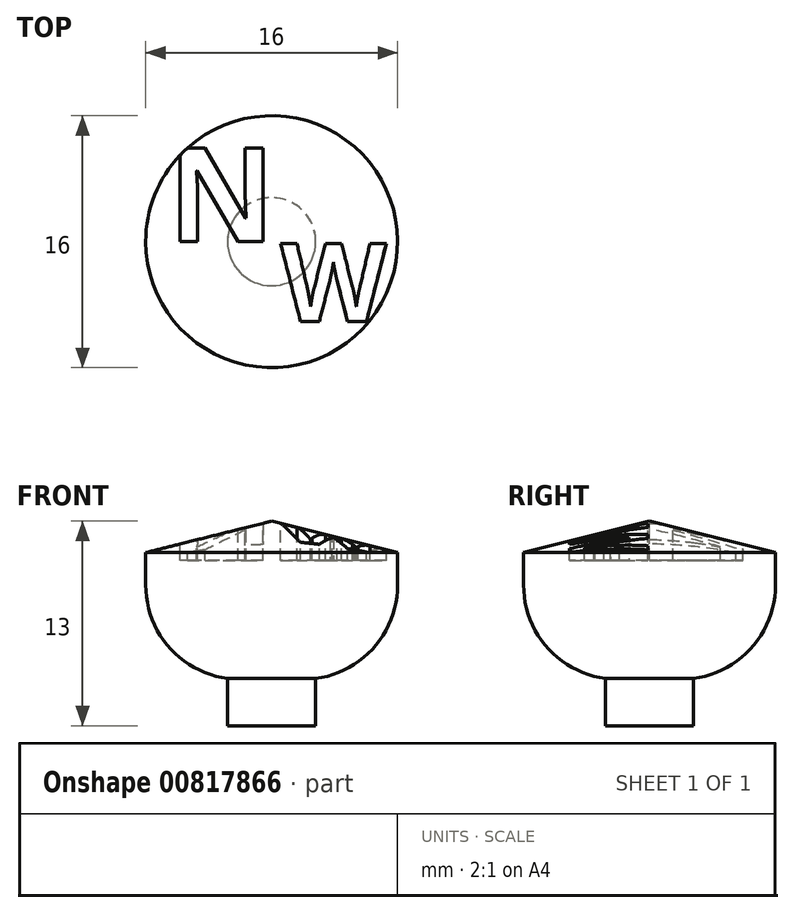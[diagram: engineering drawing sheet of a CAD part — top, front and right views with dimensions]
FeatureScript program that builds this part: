
annotation { "Feature Type Name" : "Feature", "Feature Type Description" : "" }
export const myFeature = defineFeature(function(context is Context, id is Id, definition is map)
    precondition{}
    {
        {
            var Q0;
            Q0=qCreatedBy(makeId("Top.planeOp"),FACE);
            var sketch = newSketch(context, id + "F0", { "sketchPlane" : qUnion([Q0])});
            skCircle(sketch, "E0", {"center": v(0, 0) * mm, "radius": 8 * mm});
            skCircle(sketch, "E1", {"center": v(0, 0) * mm, "radius": 2.8 * mm});
            skSolve(sketch);
        }
        {
            var Q0;
            Q0=makeQuery(id+"F0.imprint","IMPRINT",FACE,{"disambiguationData":[TD([[makeQuery(id+"F0.imprint","IMPRINT",EDGE,{"derivedFrom":sQuery(id+"F0.wireOp",EDGE,"E1")}),1.0]])]});
            extrude(context, id + "F1", {"entities" : qUnion([Q0]), "oppositeDirection" : true, "depth" : 13 * mm, "offsetDistance" : 25 * mm});
        }
        {
            var Q0;
            Q0=makeQuery(id+"F0.imprint","IMPRINT",FACE,{"disambiguationData":[TD([[makeQuery(id+"F0.imprint","IMPRINT",EDGE,{"derivedFrom":sQuery(id+"F0.wireOp",EDGE,"E0")}),1.0]])]});
            var Q1;
            Q1=makeQuery(id+"F0.imprint","IMPRINT",FACE,{"disambiguationData":[TD([[makeQuery(id+"F0.imprint","IMPRINT",EDGE,{"derivedFrom":sQuery(id+"F0.wireOp",EDGE,"E1")}),-1.0]])]});
            extrude(context, id + "F2", {"entities" : qUnion([Q0, Q1]), "operationType" : NewBodyOperationType.ADD, "oppositeDirection" : true, "depth" : 2 * mm, "offsetDistance" : 25 * mm});
        }
        {
            var Q0;
            Q0=makeQuery(id+"F0.imprint","IMPRINT",FACE,{"disambiguationData":[TD([[makeQuery(id+"F0.imprint","IMPRINT",EDGE,{"derivedFrom":sQuery(id+"F0.wireOp",EDGE,"E1")}),-1.0]])]});
            extrude(context, id + "F3", {"entities" : qUnion([Q0]), "operationType" : NewBodyOperationType.ADD, "oppositeDirection" : true, "depth" : 10 * mm, "offsetDistance" : 25 * mm});
        }
        {
            var Q0;
            Q0=makeQuery(id+"F2.opExtrude","CAP_EDGE",EDGE,{"disambiguationData":[OSD([sQuery(id+"F0.wireOp",EDGE,"E0")])],"isStart":true});
            fillet(context, id + "F4", {"entities" : qUnion([Q0]), "radius" : 1 * mm, "tangentPropagation" : true, "allowEdgeOverflow" : false});
        }
        {
            var Q0;
            Q0=qCreatedBy(makeId("Top.planeOp"),FACE);
            var sketch = newSketch(context, id + "F5", { "sketchPlane" : qUnion([Q0])});
            skText(sketch, "E2", { "text": "N", "fontName": "OpenSans-Bold.ttf"});
            skText(sketch, "E3", { "text": "W", "fontName": "OpenSans-Bold.ttf"});
            const initialGuessF5  = {"E2": [-0.00657, 0, 1, 0, 0.006], "E3": [0.00057, -0.00507, 1, 0, 0.005]};
            skSetInitialGuess(sketch, initialGuessF5);
            skSolve(sketch);
        }
        {
            var Q0;
            Q0=makeQuery(id+"F5.imprint","IMPRINT",FACE,{"disambiguationData":[TD([[makeQuery(id+"F5.imprint","IMPRINT",EDGE,{"derivedFrom":sQuery(id+"F5.wireOp",EDGE,"E2.sketch_text.stroke-0")}),-1.0]])]});
            var Q1;
            Q1=makeQuery(id+"F5.imprint","IMPRINT",FACE,{"disambiguationData":[TD([[makeQuery(id+"F5.imprint","IMPRINT",EDGE,{"derivedFrom":sQuery(id+"F5.wireOp",EDGE,"E3.sketch_text.stroke-0")}),-1.0]])]});
            extrude(context, id + "F6", {"entities" : qUnion([Q0, Q1]), "operationType" : NewBodyOperationType.REMOVE, "oppositeDirection" : true, "depth" : 2.5 * mm, "offsetDistance" : 25 * mm});
        }
        {
            var Q0;
            Q0=qCreatedBy(makeId("Front.planeOp"),FACE);
            var sketch = newSketch(context, id + "F7", { "sketchPlane" : qUnion([Q0])});
            skLineSegment(sketch, "E4", {"start": v(0, 0) * mm, "end": v(0, -9.93) * mm});
            skLineSegment(sketch, "E5", {"start": v(0, -1.56) * mm, "end": v(9.7, -1.56) * mm});
            skArc(sketch, "E6", {"start": v(0, -9.93) * mm, "mid": v(6.9, -8.11) * mm, "end": v(9.7, -1.56) * mm});
            skSolve(sketch);
        }
        {
            var Q0;
            Q0=qCreatedBy(makeId("Front.planeOp"),FACE);
            var sketch = newSketch(context, id + "F8", { "sketchPlane" : qUnion([Q0])});
            skLineSegment(sketch, "E7", {"start": v(0, 0) * mm, "end": v(10, 0) * mm});
            skLineSegment(sketch, "E8", {"start": v(10, 0) * mm, "end": v(10, -2.5) * mm});
            skLineSegment(sketch, "E9", {"start": v(10, -2.5) * mm, "end": v(0, 0) * mm});
            skLineSegment(sketch, "E10.MirrorCS", {"start": v(-10, -2.5) * mm, "end": v(0, 0) * mm});
            skLineSegment(sketch, "E11.MirrorCS", {"start": v(0, 0) * mm, "end": v(-10, 0) * mm});
            skLineSegment(sketch, "E12.MirrorCS", {"start": v(-10, 0) * mm, "end": v(-10, -2.5) * mm});
            skLineSegment(sketch, "E13", {"start": v(0, 0) * mm, "end": v(0, -10.8) * mm});
            skSolve(sketch);
        }
        {
            var Q0;
            Q0 = qSketchRegion(id + "F8", true);
            var Q1;
            Q1=sQuery(id+"F8.wireOp",EDGE,"E13");
            revolve(context, id + "F9", {"operationType" : NewBodyOperationType.REMOVE, "surfaceOperationType" : NewSurfaceOperationType.NEW, "entities" : qUnion([Q0]), "axis" : qUnion([Q1]), "revolveType" : RevolveType.SYMMETRIC, "oppositeDirection" : true, "angle" : 180 * degree});
        }
        {
            var Q0;
            Q0=makeQuery(id+"F3.opExtrude","CAP_EDGE",EDGE,{"disambiguationData":[OSD([sQuery(id+"F0.wireOp",EDGE,"E0")])],"isStart":false});
            fillet(context, id + "F10", {"entities" : qUnion([Q0]), "radius" : 6 * mm, "tangentPropagation" : true, "allowEdgeOverflow" : false});
        }
    });
